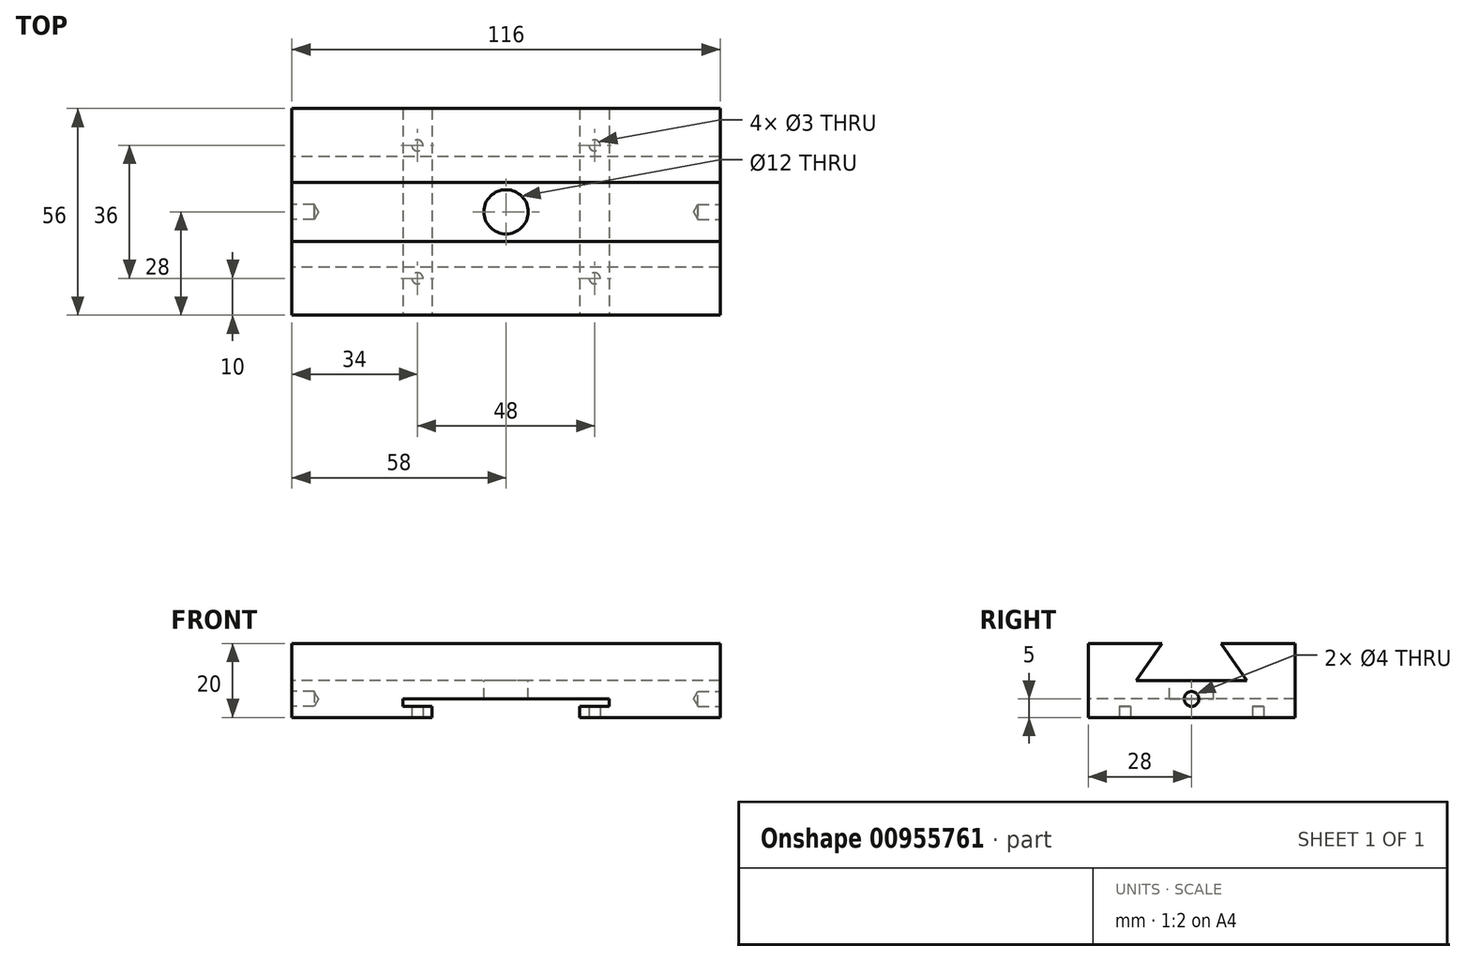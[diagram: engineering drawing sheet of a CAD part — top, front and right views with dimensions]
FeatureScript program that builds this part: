
annotation { "Feature Type Name" : "Feature", "Feature Type Description" : "" }
export const myFeature = defineFeature(function(context is Context, id is Id, definition is map)
    precondition{}
    {
        {
            var Q0;
            Q0=qCreatedBy(makeId("Front.planeOp"),FACE);
            var sketch = newSketch(context, id + "F0", { "sketchPlane" : qUnion([Q0])});
            skLineSegment(sketch, "E0", {"start": v(2, 2) * mm, "end": v(12, 2) * mm});
            skLineSegment(sketch, "E1", {"start": v(12, 2) * mm, "end": v(12.5, 0) * mm});
            skLineSegment(sketch, "E2", {"start": v(12.5, 0) * mm, "end": v(58, 0) * mm});
            skLineSegment(sketch, "E3", {"start": v(58, 0) * mm, "end": v(58, 20) * mm});
            skLineSegment(sketch, "E4", {"start": v(-58, 20) * mm, "end": v(-58, 0) * mm});
            skLineSegment(sketch, "E5", {"start": v(-58, 0) * mm, "end": v(-12.5, 0) * mm});
            skLineSegment(sketch, "E6", {"start": v(-12.5, 0) * mm, "end": v(-12, 2) * mm});
            skLineSegment(sketch, "E7", {"start": v(-12, 2) * mm, "end": v(-2, 2) * mm});
            skLineSegment(sketch, "E8", {"start": v(-58, 20) * mm, "end": v(58, 20) * mm});
            skLineSegment(sketch, "E9", {"start": v(0, 0) * mm, "end": v(-1.5, 0) * mm});
            skLineSegment(sketch, "E10", {"start": v(-1.5, 0) * mm, "end": v(-2, 2) * mm});
            skLineSegment(sketch, "E11", {"start": v(0, 0) * mm, "end": v(1.5, 0) * mm});
            skLineSegment(sketch, "E12", {"start": v(1.5, 0) * mm, "end": v(2, 2) * mm});
            skSolve(sketch);
        }
        {
            var Q0;
            Q0=makeQuery(id+"F0.imprint","IMPRINT",FACE,{"disambiguationData":[TD([[makeQuery(id+"F0.imprint","IMPRINT",EDGE,{"derivedFrom":sQuery(id+"F0.wireOp",EDGE,"zo6ZiONU-3IiS-W8wq-WPRh-nkQJYUhjSfGB")}),1.0]])]});
            var Q1;
            Q1=makeQuery(id+"F0.imprint","IMPRINT",FACE,{"disambiguationData":[TD([[makeQuery(id+"F0.imprint","IMPRINT",EDGE,{"derivedFrom":sQuery(id+"F0.wireOp",EDGE,"E0")}),1.0]])]});
            extrude(context, id + "F1", {"entities" : qUnion([Q0, Q1]), "depth" : 56 * mm});
        }
        {
            var Q0;
            Q0=makeQuery(id+"F1.opExtrude","SWEPT_FACE",FACE,{"disambiguationData":[OSD([sQuery(id+"F0.wireOp",EDGE,"E4")])]});
            var sketch = newSketch(context, id + "F2", { "sketchPlane" : qUnion([Q0])});
            skLineSegment(sketch, "E13", {"start": v(0, 20) * mm, "end": v(28, 20) * mm});
            skLineSegment(sketch, "E14", {"start": v(28, 20) * mm, "end": v(28, 10) * mm});
            skLineSegment(sketch, "E15", {"start": v(28, 10) * mm, "end": v(43, 10) * mm});
            skLineSegment(sketch, "E16", {"start": v(43, 10) * mm, "end": v(36, 20) * mm});
            skLineSegment(sketch, "E17", {"start": v(28, 10) * mm, "end": v(13, 10) * mm});
            skLineSegment(sketch, "E18", {"start": v(13, 10) * mm, "end": v(20, 20) * mm});
            skLineSegment(sketch, "E19", {"start": v(36, 20) * mm, "end": v(20, 20) * mm});
            skSolve(sketch);
        }
        {
            var Q0;
            {var subQ0=sQuery(id+"F2.wireOp",EDGE,"E14");Q0=makeQuery(id+"F2.imprint","IMPRINT",FACE,{"disambiguationData":[TD([[makeQuery(id+"F2.imprint","IMPRINT",EDGE,{"derivedFrom":subQ0}),-1.0]])]});}
            var Q1;
            {var subQ0=sQuery(id+"F2.wireOp",EDGE,"E14");Q1=makeQuery(id+"F2.imprint","IMPRINT",FACE,{"disambiguationData":[TD([[makeQuery(id+"F2.imprint","IMPRINT",EDGE,{"derivedFrom":subQ0}),1.0]])]});}
            extrude(context, id + "F3", {"entities" : qUnion([Q0, Q1]), "operationType" : NewBodyOperationType.REMOVE, "endBound" : BoundingType.UP_TO_NEXT, "oppositeDirection" : true, "depth" : 25 * mm});
        }
        {
            var Q0;
            Q0=makeQuery(id+"F3.boolean.opBoolean","COPY",FACE,{"derivedFrom":makeQuery(id+"F3.opExtrude","SWEPT_FACE",FACE,{"disambiguationData":[OSD([sQuery(id+"F2.wireOp",EDGE,"E15"),sQuery(id+"F2.wireOp",EDGE,"E17")])]})});
            var sketch = newSketch(context, id + "F4", { "sketchPlane" : qUnion([Q0])});
            skPoint(sketch, "E20", {"position": v(0, -28) * mm});
            skSolve(sketch);
        }
        {
            var Q0;
            Q0=sQuery(id+"F4.wireOp",VERTEX,"E20");
            var Q1;
            Q1=makeQuery(id+"F1.opExtrude","SWEPT_BODY",BODY,{"disambiguationData":[OSD([sQuery(id+"F0.wireOp",EDGE,"E0"),sQuery(id+"F0.wireOp",EDGE,"E1"),sQuery(id+"F0.wireOp",EDGE,"E2"),sQuery(id+"F0.wireOp",EDGE,"E3"),sQuery(id+"F0.wireOp",EDGE,"E4"),sQuery(id+"F0.wireOp",EDGE,"E5"),sQuery(id+"F0.wireOp",EDGE,"E6"),sQuery(id+"F0.wireOp",EDGE,"E7"),sQuery(id+"F0.wireOp",EDGE,"E8"),sQuery(id+"F0.wireOp",EDGE,"E9"),sQuery(id+"F0.wireOp",EDGE,"E10"),sQuery(id+"F0.wireOp",EDGE,"E11"),sQuery(id+"F0.wireOp",EDGE,"E12")])]});
            hole(context, id + "F5", {"style" : HoleStyle.SIMPLE, "endStyle" : HoleEndStyle.BLIND, "holeDiameter" : 12 * mm, "holeDepth" : 5 * mm, "isTappedThrough" : true, "tappedDepth" : 12 * mm, "tapClearance" : 3, "locations" : qUnion([Q0]), "scope" : qUnion([Q1])});
        }
        {
            var Q0;
            Q0=makeQuery(id+"F1.opExtrude","SWEPT_FACE",FACE,{"disambiguationData":[OSD([sQuery(id+"F0.wireOp",EDGE,"E4")])]});
            var sketch = newSketch(context, id + "F6", { "sketchPlane" : qUnion([Q0])});
            skPoint(sketch, "E21", {"position": v(28, 5) * mm});
            skSolve(sketch);
        }
        {
            var Q0;
            Q0=sQuery(id+"F6.wireOp",VERTEX,"E21");
            var Q1;
            Q1=makeQuery(id+"F1.opExtrude","SWEPT_BODY",BODY,{"disambiguationData":[OSD([sQuery(id+"F0.wireOp",EDGE,"E0"),sQuery(id+"F0.wireOp",EDGE,"E1"),sQuery(id+"F0.wireOp",EDGE,"E2"),sQuery(id+"F0.wireOp",EDGE,"E3"),sQuery(id+"F0.wireOp",EDGE,"E4"),sQuery(id+"F0.wireOp",EDGE,"E5"),sQuery(id+"F0.wireOp",EDGE,"E6"),sQuery(id+"F0.wireOp",EDGE,"E7"),sQuery(id+"F0.wireOp",EDGE,"E8"),sQuery(id+"F0.wireOp",EDGE,"E9"),sQuery(id+"F0.wireOp",EDGE,"E10"),sQuery(id+"F0.wireOp",EDGE,"E11"),sQuery(id+"F0.wireOp",EDGE,"E12")])]});
            hole(context, id + "F7", {"style" : HoleStyle.SIMPLE, "endStyle" : HoleEndStyle.BLIND, "holeDiameter" : 4 * mm, "holeDepth" : 6 * mm, "isTappedThrough" : true, "tappedDepth" : 12 * mm, "tapClearance" : 3, "startFromSketch" : true, "locations" : qUnion([Q0]), "scope" : qUnion([Q1])});
        }
        {
            var Q0;
            Q0=makeQuery(id+"F1.opExtrude","SWEPT_FACE",FACE,{"disambiguationData":[OSD([sQuery(id+"F0.wireOp",EDGE,"E3")])]});
            var sketch = newSketch(context, id + "F8", { "sketchPlane" : qUnion([Q0])});
            skPoint(sketch, "E22", {"position": v(-28, 5) * mm});
            skSolve(sketch);
        }
        {
            var Q0;
            Q0=sQuery(id+"F8.wireOp",VERTEX,"E22");
            var Q1;
            Q1=makeQuery(id+"F1.opExtrude","SWEPT_BODY",BODY,{"disambiguationData":[OSD([sQuery(id+"F0.wireOp",EDGE,"E0"),sQuery(id+"F0.wireOp",EDGE,"E1"),sQuery(id+"F0.wireOp",EDGE,"E2"),sQuery(id+"F0.wireOp",EDGE,"E3"),sQuery(id+"F0.wireOp",EDGE,"E4"),sQuery(id+"F0.wireOp",EDGE,"E5"),sQuery(id+"F0.wireOp",EDGE,"E6"),sQuery(id+"F0.wireOp",EDGE,"E7"),sQuery(id+"F0.wireOp",EDGE,"E8"),sQuery(id+"F0.wireOp",EDGE,"E9"),sQuery(id+"F0.wireOp",EDGE,"E10"),sQuery(id+"F0.wireOp",EDGE,"E11"),sQuery(id+"F0.wireOp",EDGE,"E12")])]});
            hole(context, id + "F9", {"style" : HoleStyle.SIMPLE, "endStyle" : HoleEndStyle.BLIND, "holeDiameter" : 4 * mm, "holeDepth" : 6 * mm, "isTappedThrough" : true, "tappedDepth" : 12 * mm, "tapClearance" : 3, "startFromSketch" : true, "locations" : qUnion([Q0]), "scope" : qUnion([Q1])});
        }
        {
            var Q0;
            Q0=makeQuery(id+"F1.opExtrude","CAP_FACE",FACE,{"disambiguationData":[OSD([sQuery(id+"F0.wireOp",EDGE,"E0"),sQuery(id+"F0.wireOp",EDGE,"E1"),sQuery(id+"F0.wireOp",EDGE,"E2"),sQuery(id+"F0.wireOp",EDGE,"E3"),sQuery(id+"F0.wireOp",EDGE,"E4"),sQuery(id+"F0.wireOp",EDGE,"E5"),sQuery(id+"F0.wireOp",EDGE,"E6"),sQuery(id+"F0.wireOp",EDGE,"E7"),sQuery(id+"F0.wireOp",EDGE,"E8"),sQuery(id+"F0.wireOp",EDGE,"E9"),sQuery(id+"F0.wireOp",EDGE,"E10"),sQuery(id+"F0.wireOp",EDGE,"E11"),sQuery(id+"F0.wireOp",EDGE,"E12")])],"isStart":false});
            var sketch = newSketch(context, id + "F10", { "sketchPlane" : qUnion([Q0])});
            skLineSegment(sketch, "E23", {"start": v(20, 0) * mm, "end": v(20, 3) * mm});
            skLineSegment(sketch, "E24", {"start": v(20, 3) * mm, "end": v(28, 3) * mm});
            skLineSegment(sketch, "E25", {"start": v(28, 3) * mm, "end": v(28, 5) * mm});
            skLineSegment(sketch, "E26", {"start": v(28, 5) * mm, "end": v(20, 5) * mm});
            skLineSegment(sketch, "E27", {"start": v(20, 5) * mm, "end": v(20, 5) * mm});
            skLineSegment(sketch, "E28", {"start": v(20, 5) * mm, "end": v(0, 5) * mm});
            skLineSegment(sketch, "E29", {"start": v(0, 5) * mm, "end": v(0, 0) * mm});
            skLineSegment(sketch, "E30", {"start": v(0, 0) * mm, "end": v(20, 0) * mm});
            skLineSegment(sketch, "E31.MirrorCS", {"start": v(-20, 5) * mm, "end": v(0, 5) * mm});
            skLineSegment(sketch, "E32.MirrorCS", {"start": v(-20, 5) * mm, "end": v(-20, 5) * mm});
            skLineSegment(sketch, "E33.MirrorCS", {"start": v(-28, 5) * mm, "end": v(-20, 5) * mm});
            skLineSegment(sketch, "E34.MirrorCS", {"start": v(-28, 3) * mm, "end": v(-28, 5) * mm});
            skLineSegment(sketch, "E35.MirrorCS", {"start": v(-20, 3) * mm, "end": v(-28, 3) * mm});
            skLineSegment(sketch, "E36.MirrorCS", {"start": v(-20, 0) * mm, "end": v(-20, 3) * mm});
            skLineSegment(sketch, "E37.MirrorCS", {"start": v(0, 0) * mm, "end": v(-20, 0) * mm});
            skSolve(sketch);
        }
        {
            var Q0;
            {var subQ2=sQuery(id+"F10.wireOp",EDGE,"E23");Q0=makeQuery(id+"F10.imprint","IMPRINT",FACE,{"disambiguationData":[TD([[makeQuery(id+"F10.imprint","IMPRINT",EDGE,{"derivedFrom":subQ2}),1.0]])]});}
            var Q1;
            {var subQ2=sQuery(id+"F10.wireOp",EDGE,"E29");Q1=makeQuery(id+"F10.imprint","IMPRINT",FACE,{"disambiguationData":[TD([[makeQuery(id+"F10.imprint","IMPRINT",EDGE,{"derivedFrom":subQ2}),-1.0]])]});}
            extrude(context, id + "F11", {"entities" : qUnion([Q0, Q1]), "operationType" : NewBodyOperationType.REMOVE, "endBound" : BoundingType.THROUGH_ALL, "oppositeDirection" : true, "depth" : 25 * mm, "offsetDistance" : 25 * mm});
        }
        {
            var Q0;
            Q0=makeQuery(id+"F1.opExtrude","SWEPT_FACE",FACE,{"disambiguationData":[OSD([sQuery(id+"F0.wireOp",EDGE,"E5")])]});
            var sketch = newSketch(context, id + "F12", { "sketchPlane" : qUnion([Q0])});
            skPoint(sketch, "E38", {"position": v(-24, 46) * mm});
            skPoint(sketch, "E39", {"position": v(-24, 10) * mm});
            skPoint(sketch, "E40.MirrorP", {"position": v(24, 46) * mm});
            skPoint(sketch, "E41.MirrorP", {"position": v(24, 10) * mm});
            skSolve(sketch);
        }
        {
            var Q0;
            Q0=sQuery(id+"F12.wireOp",VERTEX,"E38");
            var Q1;
            Q1=sQuery(id+"F12.wireOp",VERTEX,"E40.MirrorP");
            var Q2;
            Q2=sQuery(id+"F12.wireOp",VERTEX,"E41.MirrorP");
            var Q3;
            Q3=sQuery(id+"F12.wireOp",VERTEX,"E39");
            var Q4;
            Q4=makeQuery(id+"F1.opExtrude","SWEPT_BODY",BODY,{"disambiguationData":[OSD([sQuery(id+"F0.wireOp",EDGE,"E0"),sQuery(id+"F0.wireOp",EDGE,"E1"),sQuery(id+"F0.wireOp",EDGE,"E2"),sQuery(id+"F0.wireOp",EDGE,"E3"),sQuery(id+"F0.wireOp",EDGE,"E4"),sQuery(id+"F0.wireOp",EDGE,"E5"),sQuery(id+"F0.wireOp",EDGE,"E6"),sQuery(id+"F0.wireOp",EDGE,"E7"),sQuery(id+"F0.wireOp",EDGE,"E8"),sQuery(id+"F0.wireOp",EDGE,"E9"),sQuery(id+"F0.wireOp",EDGE,"E10"),sQuery(id+"F0.wireOp",EDGE,"E11"),sQuery(id+"F0.wireOp",EDGE,"E12")])]});
            hole(context, id + "F13", {"style" : HoleStyle.SIMPLE, "endStyle" : HoleEndStyle.BLIND, "holeDiameter" : 3 * mm, "majorDiameter" : 5 * mm, "holeDepth" : 4 * mm, "isTappedThrough" : true, "tappedDepth" : 12 * mm, "tapClearance" : 3, "locations" : qUnion([Q0, Q1, Q2, Q3]), "scope" : qUnion([Q4])});
        }
    });
